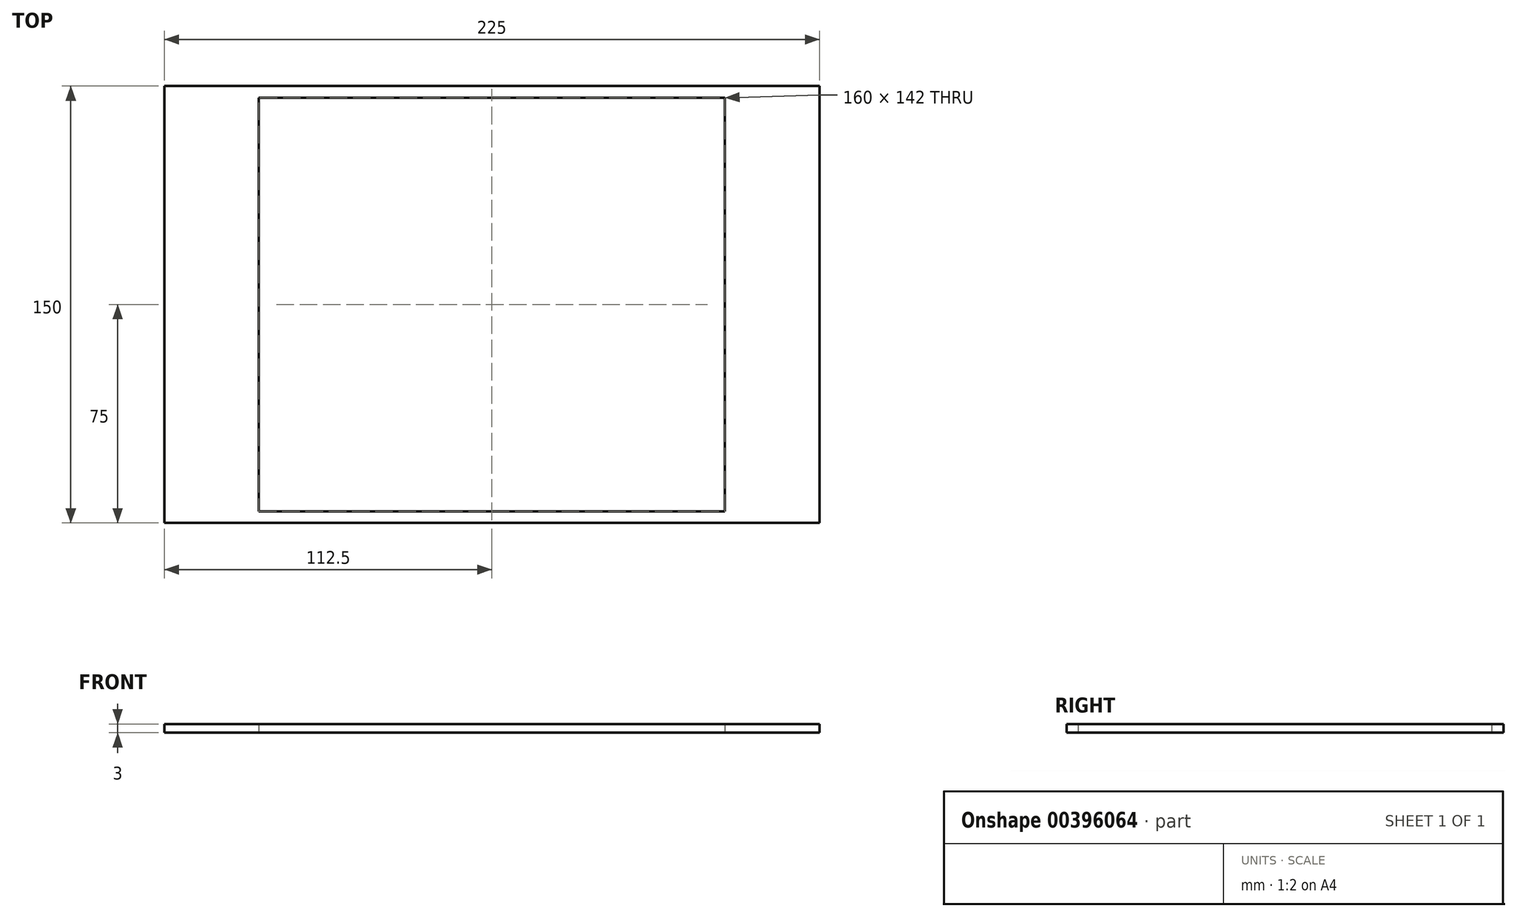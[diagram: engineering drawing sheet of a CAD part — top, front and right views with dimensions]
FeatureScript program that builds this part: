
annotation { "Feature Type Name" : "Feature", "Feature Type Description" : "" }
export const myFeature = defineFeature(function(context is Context, id is Id, definition is map)
    precondition{}
    {
        {
            var Q0;
            Q0=qCreatedBy(makeId("Top.planeOp"),FACE);
            var sketch = newSketch(context, id + "F0", { "sketchPlane" : qUnion([Q0])});
            skPoint(sketch, "E0.middle", {"position": v(0, 0) * mm});
            skPoint(sketch, "E1.visualSharp", {"position": v(-137.5, 105) * mm});
            skPoint(sketch, "E2.visualSharp", {"position": v(-137.5, -105) * mm});
            skPoint(sketch, "E3.visualSharp", {"position": v(137.5, -105) * mm});
            skPoint(sketch, "E4.visualSharp", {"position": v(137.5, 105) * mm});
            skLineSegment(sketch, "E5.bottom", {"start": v(-112.5, 75) * mm, "end": v(112.5, 75) * mm});
            skLineSegment(sketch, "E5.top", {"start": v(-112.5, -75) * mm, "end": v(112.5, -75) * mm});
            skLineSegment(sketch, "E5.left", {"start": v(-112.5, 75) * mm, "end": v(-112.5, -75) * mm});
            skLineSegment(sketch, "E5.right", {"start": v(112.5, 75) * mm, "end": v(112.5, -75) * mm});
            skLineSegment(sketch, "E6.bottom", {"start": v(-80, 71) * mm, "end": v(80, 71) * mm});
            skLineSegment(sketch, "E6.top", {"start": v(-80, -71) * mm, "end": v(80, -71) * mm});
            skLineSegment(sketch, "E6.left", {"start": v(-80, 71) * mm, "end": v(-80, -71) * mm});
            skLineSegment(sketch, "E6.right", {"start": v(80, 71) * mm, "end": v(80, -71) * mm});
            skSolve(sketch);
        }
        {
            var Q0;
            Q0=qSketchRegion(id+"F0",true);
            extrude(context, id + "F1", {"entities" : qUnion([Q0]), "depth" : 3 * mm});
        }
    });
